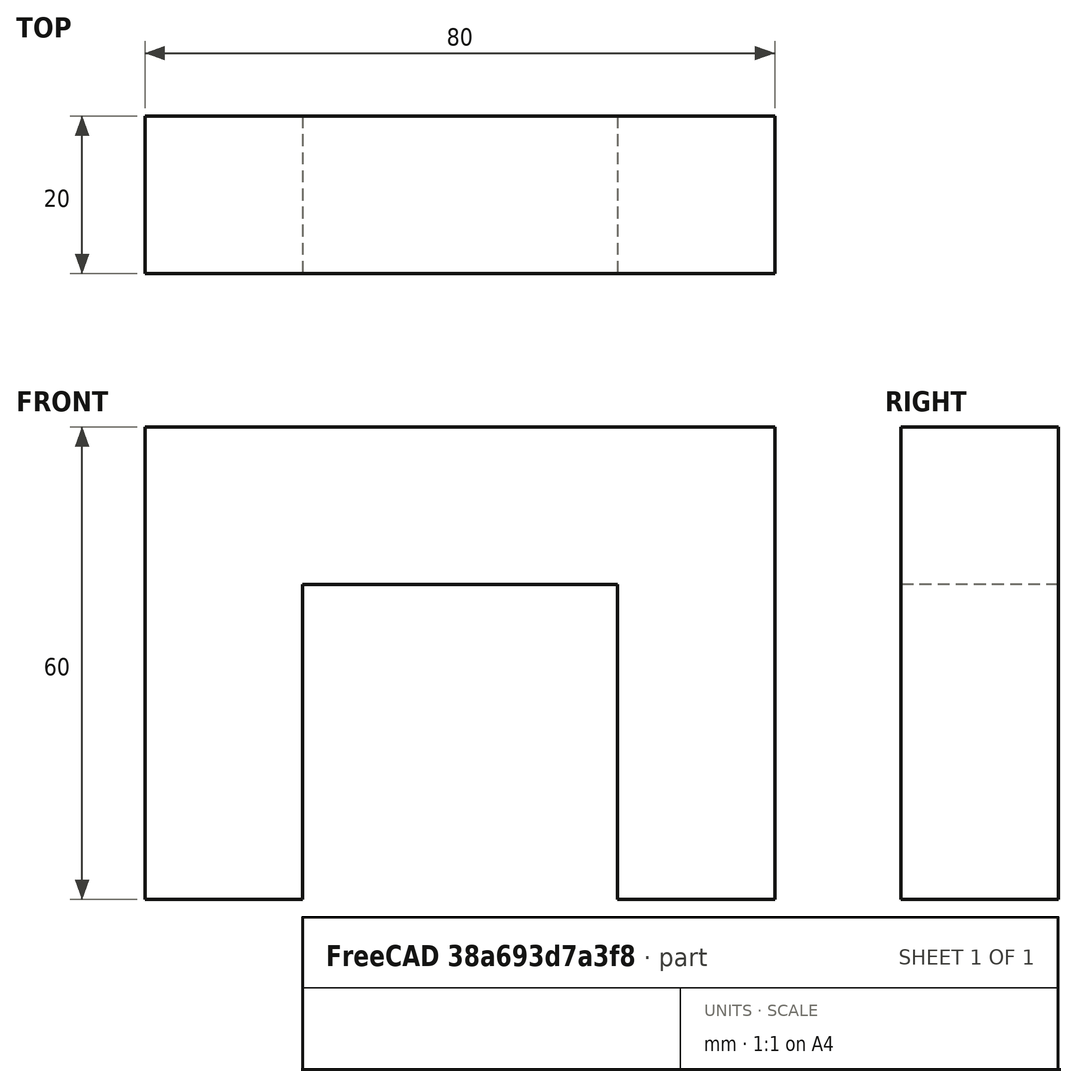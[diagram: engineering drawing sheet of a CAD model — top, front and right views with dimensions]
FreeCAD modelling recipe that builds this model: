
FCSTD DOCUMENT  (FreeCAD 0.17R10760 (Git))
Label: bridge
License: All rights reserved
LicenseURL: http://en.wikipedia.org/wiki/All_rights_reserved
objects: Sketcher::SketchObject×1, PartDesign::Pad×1, PartDesign::Body×1, TechDraw::DrawSVGTemplate×1, TechDraw::DrawProjGroupItem×1, TechDraw::DrawProjGroup×1, TechDraw::DrawViewPart×1, TechDraw::DrawPage×1
note: 4 computed .brp shape members not serialized (recipe doc carries the construction recipe); baked Part::Feature solids carry a one-line shape summary decoded from their .brp

FEATURE [Sketcher::SketchObject] Sketch
  MapMode = 5
  Placement = pos=(0,0,0) rot=(1,0,0;1.5708rad)
  Support = -> [XZ_Plane]
  sketch-geometry (8):
    g0: LineSegment StartX=-40 StartY=0 StartZ=0 EndX=-20 EndY=0 EndZ=0
    g1: LineSegment StartX=-20 StartY=0 StartZ=0 EndX=-20 EndY=40 EndZ=0
    g2: LineSegment StartX=-20 StartY=40 StartZ=0 EndX=20 EndY=40 EndZ=0
    g3: LineSegment StartX=20 StartY=40 StartZ=0 EndX=20 EndY=0 EndZ=0
    g4: LineSegment StartX=20 StartY=0 StartZ=0 EndX=40 EndY=0 EndZ=0
    g5: LineSegment StartX=40 StartY=0 StartZ=0 EndX=40 EndY=60 EndZ=0
    g6: LineSegment StartX=40 StartY=60 StartZ=0 EndX=-40 EndY=60 EndZ=0
    g7: LineSegment StartX=-40 StartY=60 StartZ=0 EndX=-40 EndY=0 EndZ=0
  constraints (23):
    c: Horizontal(g0)
    c: Coincident(g0,g1)
    c: Vertical(g1)
    c: Coincident(g1,g2)
    c: Horizontal(g2)
    c: Coincident(g2,g3)
    c: Vertical(g3)
    c: Coincident(g3,g4)
    c: Horizontal(g4)
    c: Coincident(g4,g5)
    c: Vertical(g5)
    c: Coincident(g5,g6)
    c: Horizontal(g6)
    c: Coincident(g6,g7)
    c: Coincident(g7,g0)
    c: Vertical(g7)
    c: Equal(g0,g4)
    c: Symmetric(g0,g3,g-1)
    c: PointOnObject(g4,g-1)
    c: DistanceX(g0,g0) = 20
    c: DistanceX(g2,g2) = 40
    c: DistanceY(g2,g5) = 20
    c: DistanceY(g3,g2) = 40
FEATURE [PartDesign::Pad] Pad
  Length = 20
  Length2 = 100
  Midplane = true
  Placement = pos=(0,0,0) rot=(1,0,0;1.5708rad)
  Profile = -> Sketch
  Type = 0
FEATURE [PartDesign::Body] Body
  Group = -> [Sketch,Pad]
  Origin = -> BodyOrigin
  Tip = -> Pad
FEATURE [TechDraw::DrawSVGTemplate] Template
  EditableTexts = Designed_by_Name=Designed by Name; Drawing_number=Drawing number; FC-Date=Date; FC-SC=Scale; FC-SH=Sheet; FC-Title=Title; Subtitle=Subtitle; Weight=Weight
  Height = 210
  Orientation = 1
  Width = 297
FEATURE [TechDraw::DrawProjGroupItem] ProjItem  label="Front"
  ArcCenterMarks = true
  CenterScale = 2
  Direction = (0,-1,0)
  HardHidden = false
  HiddenWidth = 0.15
  HorizCenterLine = false
  IsoCount = 0
  IsoHidden = false
  IsoVisible = false
  IsoWidth = 0.3
  KeepLabel = false
  LineWidth = 0.7
  Rotation = 0
  RotationVector = (1,0,0)
  ScaleType = 0
  SeamHidden = false
  SeamVisible = false
  ShowSectionLine = true
  SmoothHidden = false
  SmoothVisible = false
  Source = -> Pad
  Type = 0
  VertCenterLine = false
  X = 0
  Y = 0
FEATURE [TechDraw::DrawProjGroup] ProjGroup
  Anchor = -> ProjItem
  AutoDistribute = true
  KeepLabel = false
  ProjectionType = 0
  Rotation = 0
  ScaleType = 0
  Source = -> Pad
  Views = -> [ProjItem]
  X = 222.605
  Y = 113.838
  spacingX = 15
  spacingY = 15
FEATURE [TechDraw::DrawViewPart] View
  ArcCenterMarks = true
  CenterScale = 2
  Direction = (1,-1,1)
  HardHidden = false
  HiddenWidth = 0.15
  HorizCenterLine = false
  IsoCount = 0
  IsoHidden = false
  IsoVisible = false
  IsoWidth = 0.3
  KeepLabel = false
  LineWidth = 0.7
  Rotation = 0
  ScaleType = 2
  SeamHidden = false
  SeamVisible = false
  ShowSectionLine = true
  SmoothHidden = false
  SmoothVisible = false
  Source = -> Pad
  VertCenterLine = false
  X = 95.8106
  Y = 116.558
FEATURE [TechDraw::DrawPage] Page
  ProjectionType = 0
  Template = -> Template
  Views = -> [ProjGroup,View]
